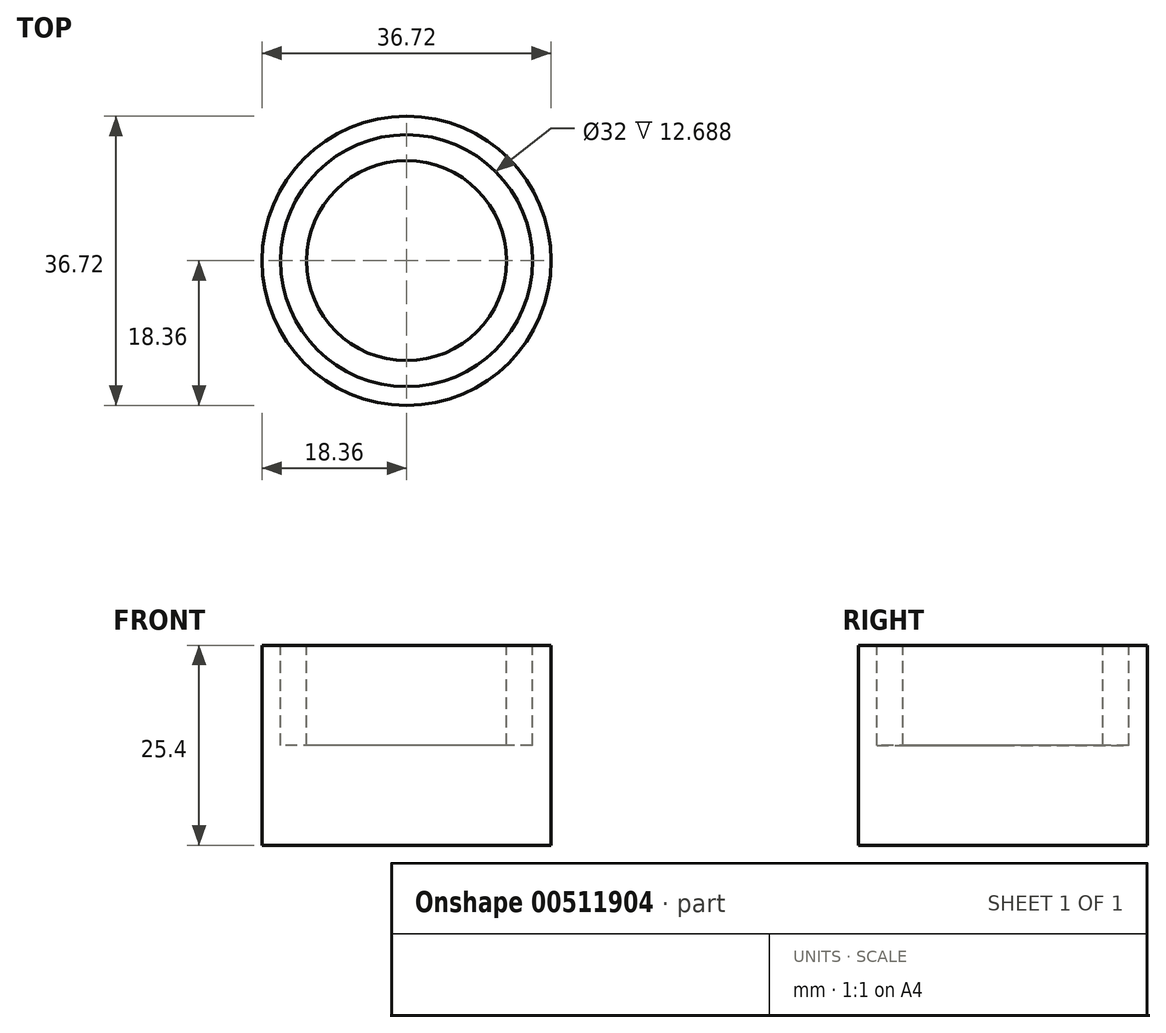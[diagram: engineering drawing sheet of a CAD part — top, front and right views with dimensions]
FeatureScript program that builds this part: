
annotation { "Feature Type Name" : "Feature", "Feature Type Description" : "" }
export const myFeature = defineFeature(function(context is Context, id is Id, definition is map)
    precondition{}
    {
        {
            var Q0;
            Q0=qCreatedBy(makeId("Front.planeOp"),FACE);
            var sketch = newSketch(context, id + "F0", { "sketchPlane" : qUnion([Q0])});
            skLineSegment(sketch, "E0", {"start": v(0, 11.12) * mm, "end": v(0, 0) * mm});
            skSolve(sketch);
        }
        {
            var Q0;
            Q0=qCreatedBy(makeId("Front.planeOp"),FACE);
            var sketch = newSketch(context, id + "F1", { "sketchPlane" : qUnion([Q0])});
            skLineSegment(sketch, "E1", {"start": v(12.7, 25.4) * mm, "end": v(12.7, 12.7) * mm});
            skLineSegment(sketch, "E2", {"start": v(18.36, 0) * mm, "end": v(18.36, 12.7) * mm});
            skLineSegment(sketch, "E3", {"start": v(12.7, 12.7) * mm, "end": v(16, 12.7) * mm});
            skLineSegment(sketch, "E4", {"start": v(12.7, 25.4) * mm, "end": v(12.7, 25.4) * mm});
            skLineSegment(sketch, "E5", {"start": v(12.7, 25.4) * mm, "end": v(0, 25.4) * mm});
            skLineSegment(sketch, "E6", {"start": v(0, 25.4) * mm, "end": v(0, 0) * mm});
            skPoint(sketch, "E7.MirrorCS.end.orphan", {"position": v(18.36, 0) * mm});
            skLineSegment(sketch, "E8", {"start": v(0, 0) * mm, "end": v(18.36, 0) * mm});
            skLineSegment(sketch, "E9", {"start": v(18.36, 12.7) * mm, "end": v(18.36, 0) * mm});
            skLineSegment(sketch, "E10.top", {"start": v(18.36, 25.39) * mm, "end": v(16, 25.39) * mm});
            skLineSegment(sketch, "E10.left", {"start": v(18.36, 12.7) * mm, "end": v(18.36, 25.39) * mm});
            skLineSegment(sketch, "E10.right", {"start": v(16, 12.7) * mm, "end": v(16, 25.39) * mm});
            skSolve(sketch);
        }
        {
            var Q0;
            Q0=makeQuery(id+"F1.imprint","IMPRINT",FACE,{"disambiguationData":[TD([[makeQuery(id+"F1.imprint","IMPRINT",EDGE,{"derivedFrom":sQuery(id+"F1.wireOp",EDGE,"E3")}),-1.0]])]});
            var Q1;
            Q1=sQuery(id+"F0.wireOp",EDGE,"E0");
            revolve(context, id + "F2", {"entities" : qUnion([Q0]), "axis" : qUnion([Q1]), "revolveType" : RevolveType.FULL});
        }
    });
